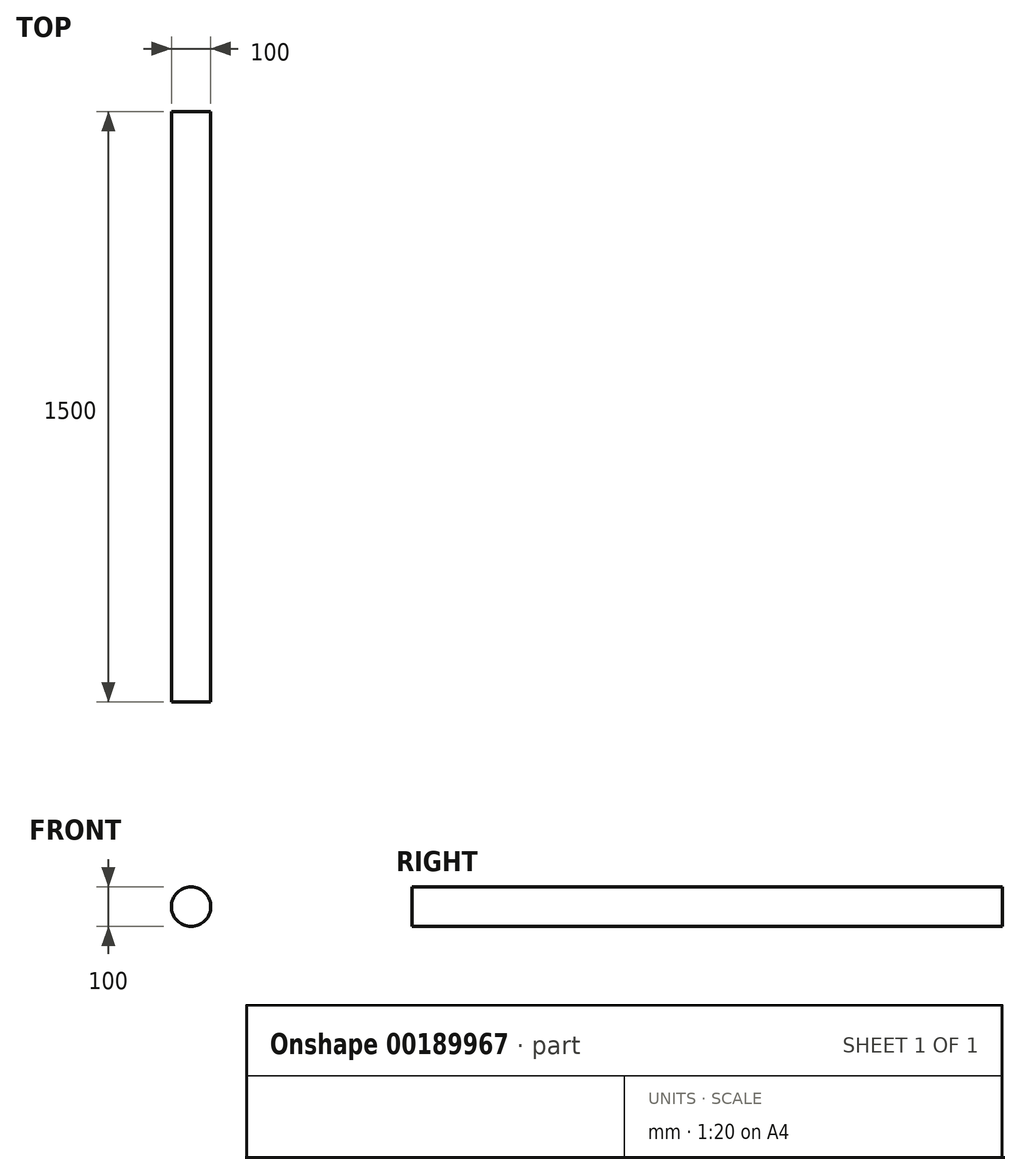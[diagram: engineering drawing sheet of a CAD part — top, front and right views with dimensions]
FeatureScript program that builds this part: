
annotation { "Feature Type Name" : "Feature", "Feature Type Description" : "" }
export const myFeature = defineFeature(function(context is Context, id is Id, definition is map)
    precondition{}
    {
        {
            var Q0;
            Q0=qCreatedBy(makeId("Front.planeOp"),FACE);
            var sketch = newSketch(context, id + "F0", { "sketchPlane" : qUnion([Q0])});
            skCircle(sketch, "E0", {"center": v(0, 0) * mm, "radius": 50 * mm});
            skSolve(sketch);
        }
        {
            var Q0;
            Q0 = qSketchRegion(id + "F0", true);
            extrude(context, id + "F1", {"entities" : qUnion([Q0]), "depth" : 1500 * mm, "offsetDistance" : 25 * mm});
        }
    });
